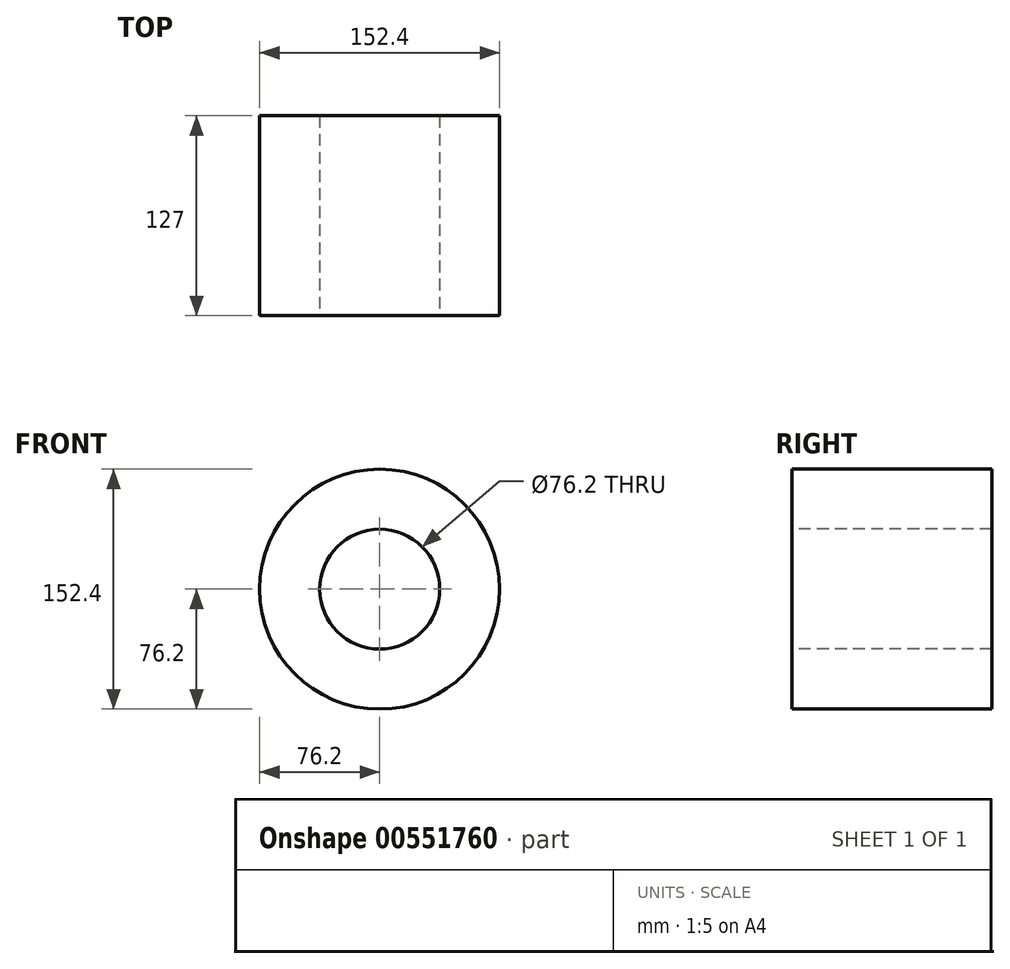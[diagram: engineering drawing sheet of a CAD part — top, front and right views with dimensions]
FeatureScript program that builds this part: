
annotation { "Feature Type Name" : "Feature", "Feature Type Description" : "" }
export const myFeature = defineFeature(function(context is Context, id is Id, definition is map)
    precondition{}
    {
        {
            var Q0;
            Q0=qCreatedBy(makeId("Front.planeOp"),FACE);
            var sketch = newSketch(context, id + "F0", { "sketchPlane" : qUnion([Q0])});
            skCircle(sketch, "E0", {"center": v(0, 0) * mm, "radius": 76.2 * mm});
            skSolve(sketch);
        }
        {
            var Q0;
            Q0 = qSketchRegion(id + "F0", true);
            extrude(context, id + "F1", {"entities" : qUnion([Q0]), "depth" : 127 * mm, "offsetDistance" : 25.4 * mm});
        }
        {
            var Q0;
            Q0=makeQuery(id+"F1.opExtrude","CAP_FACE",FACE,{"disambiguationData":[OSD([sQuery(id+"F0.wireOp",EDGE,"E0")])],"isStart":false});
            var sketch = newSketch(context, id + "F2", { "sketchPlane" : qUnion([Q0])});
            skCircle(sketch, "E1", {"center": v(0, 0) * mm, "radius": 38.1 * mm});
            skSolve(sketch);
        }
        {
            var Q0;
            Q0=sQuery(id+"F2.wireOp",VERTEX,"E1.center");
            var Q1;
            Q1=makeQuery(id+"F1.opExtrude","SWEPT_BODY",BODY,{"disambiguationData":[OSD([sQuery(id+"F0.wireOp",EDGE,"E0")])]});
            hole(context, id + "F3", {"style" : HoleStyle.SIMPLE, "endStyle" : HoleEndStyle.THROUGH, "holeDiameter" : 76.2 * mm, "isTappedThrough" : true, "tappedDepth" : 12.7 * mm, "tapClearance" : 3, "locations" : qUnion([Q0]), "scope" : qUnion([Q1])});
        }
    });
